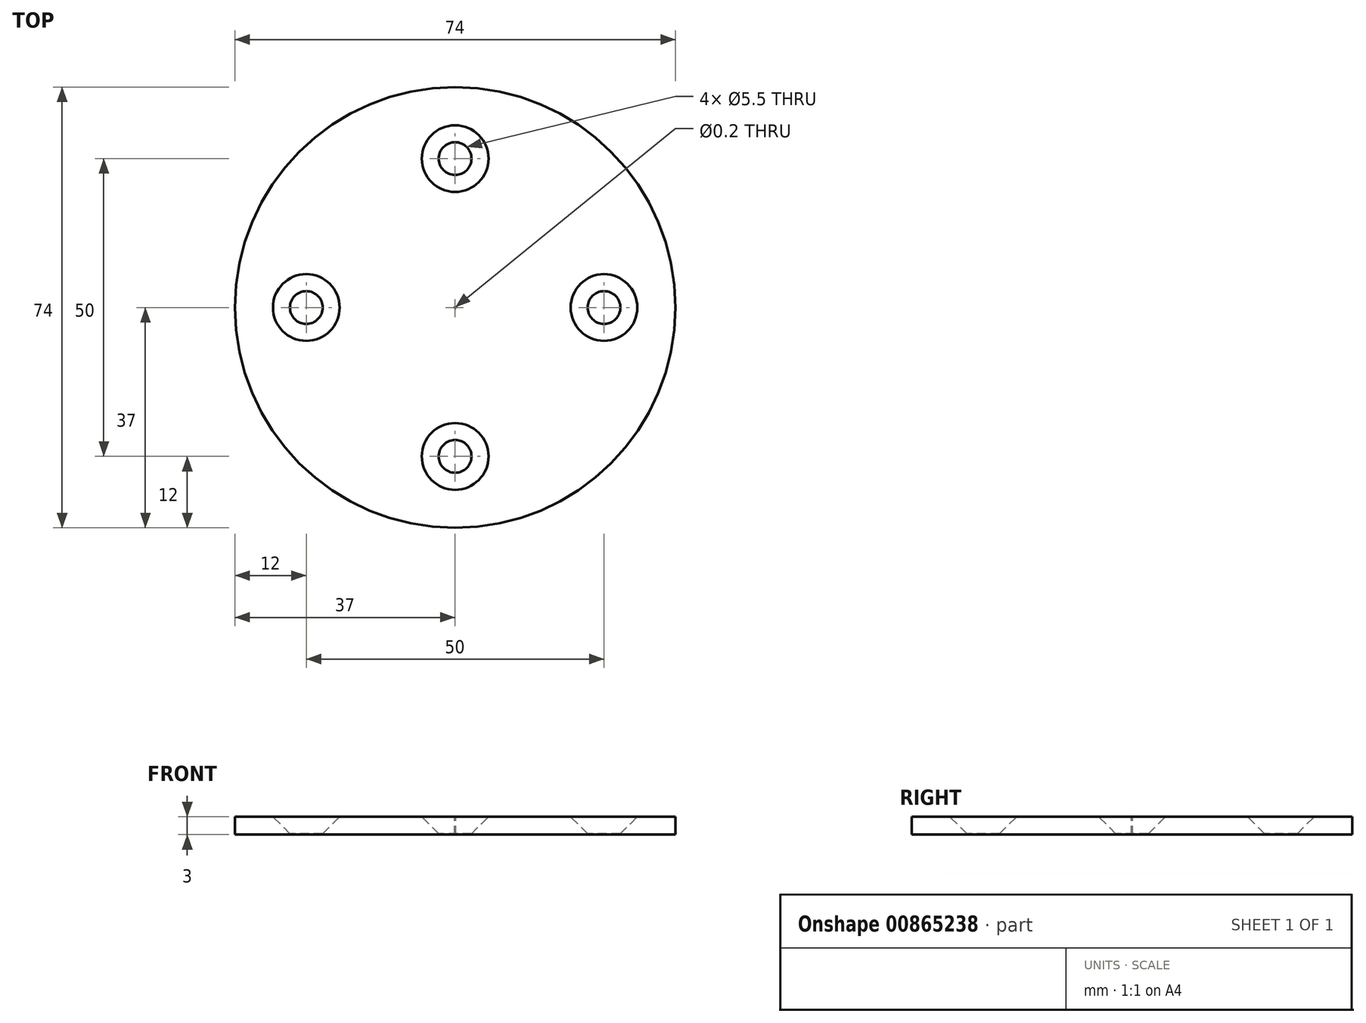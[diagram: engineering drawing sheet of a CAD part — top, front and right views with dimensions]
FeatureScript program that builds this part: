
annotation { "Feature Type Name" : "Feature", "Feature Type Description" : "" }
export const myFeature = defineFeature(function(context is Context, id is Id, definition is map)
    precondition{}
    {
        {
            var Q0;
            Q0=qCreatedBy(makeId("Top.planeOp"),FACE);
            var sketch = newSketch(context, id + "F0", { "sketchPlane" : qUnion([Q0])});
            skCircle(sketch, "E0", {"center": v(0, 0) * mm, "radius": 37 * mm});
            skSolve(sketch);
        }
        {
            var Q0;
            Q0=makeQuery(id+"F0.imprint","IMPRINT",FACE,{"disambiguationData":[TD([[makeQuery(id+"F0.imprint","IMPRINT",EDGE,{"derivedFrom":sQuery(id+"F0.wireOp",EDGE,"E0")}),1.0]])]});
            extrude(context, id + "F1", {"entities" : qUnion([Q0]), "depth" : 3 * mm, "offsetDistance" : 25 * mm});
        }
        {
            var Q0;
            Q0=makeQuery(id+"F1.opExtrude","CAP_FACE",FACE,{"disambiguationData":[OSD([sQuery(id+"F0.wireOp",EDGE,"E0")])],"isStart":false});
            var sketch = newSketch(context, id + "F2", { "sketchPlane" : qUnion([Q0])});
            skCircle(sketch, "E1", {"center": v(0, 0) * mm, "radius": 25 * mm});
            skPoint(sketch, "E2", {"position": v(-25, 0) * mm});
            skPoint(sketch, "E3", {"position": v(0, 25) * mm});
            skPoint(sketch, "E4", {"position": v(25, 0) * mm});
            skPoint(sketch, "E5", {"position": v(0, -25) * mm});
            skSolve(sketch);
        }
        {
            var Q0;
            Q0=sQuery(id+"F2.wireOp",VERTEX,"E3");
            var Q1;
            Q1=sQuery(id+"F2.wireOp",VERTEX,"E2");
            var Q2;
            Q2=sQuery(id+"F2.wireOp",VERTEX,"E5");
            var Q3;
            Q3=sQuery(id+"F2.wireOp",VERTEX,"E4");
            var Q4;
            Q4=makeQuery(id+"F1.opExtrude","SWEPT_BODY",BODY,{"disambiguationData":[OSD([sQuery(id+"F0.wireOp",EDGE,"E0")])]});
            hole(context, id + "F3", {"style" : HoleStyle.C_SINK, "endStyle" : HoleEndStyle.BLIND, "standardTappedOrClearance" : lookupTablePath({ "fit" : "Normal", "standard" : "ISO", "size" : "M5", "type" : "Clearance" }), "standardBlindInLast" : lookupTablePath({ "fit" : "Standard", "standard" : "ISO", "size" : "M5", "type" : "Clearance" }), "holeDiameter" : 5.5 * mm, "cSinkDiameter" : 11.2 * mm, "cSinkAngle" : 90 * degree, "majorDiameter" : 5 * mm, "holeDepth" : 15 * mm, "isTappedThrough" : true, "tappedDepth" : 12 * mm, "tapClearance" : 3, "locations" : qUnion([Q0, Q1, Q2, Q3]), "scope" : qUnion([Q4])});
        }
        {
            var Q0;
            Q0=makeQuery(id+"F1.opExtrude","CAP_FACE",FACE,{"disambiguationData":[OSD([sQuery(id+"F0.wireOp",EDGE,"E0")])],"isStart":false});
            var sketch = newSketch(context, id + "F4", { "sketchPlane" : qUnion([Q0])});
            skPoint(sketch, "E6", {"position": v(0, 0) * mm});
            skSolve(sketch);
        }
        {
            var Q0;
            Q0=sQuery(id+"F4.wireOp",VERTEX,"E6");
            var Q1;
            Q1=makeQuery(id+"F1.opExtrude","SWEPT_BODY",BODY,{"disambiguationData":[OSD([sQuery(id+"F0.wireOp",EDGE,"E0")])]});
            hole(context, id + "F5", {"style" : HoleStyle.SIMPLE, "endStyle" : HoleEndStyle.THROUGH, "holeDiameter" : 0.2 * mm, "majorDiameter" : 5 * mm, "isTappedThrough" : true, "tappedDepth" : 12 * mm, "tapClearance" : 3, "locations" : qUnion([Q0]), "scope" : qUnion([Q1])});
        }
    });
